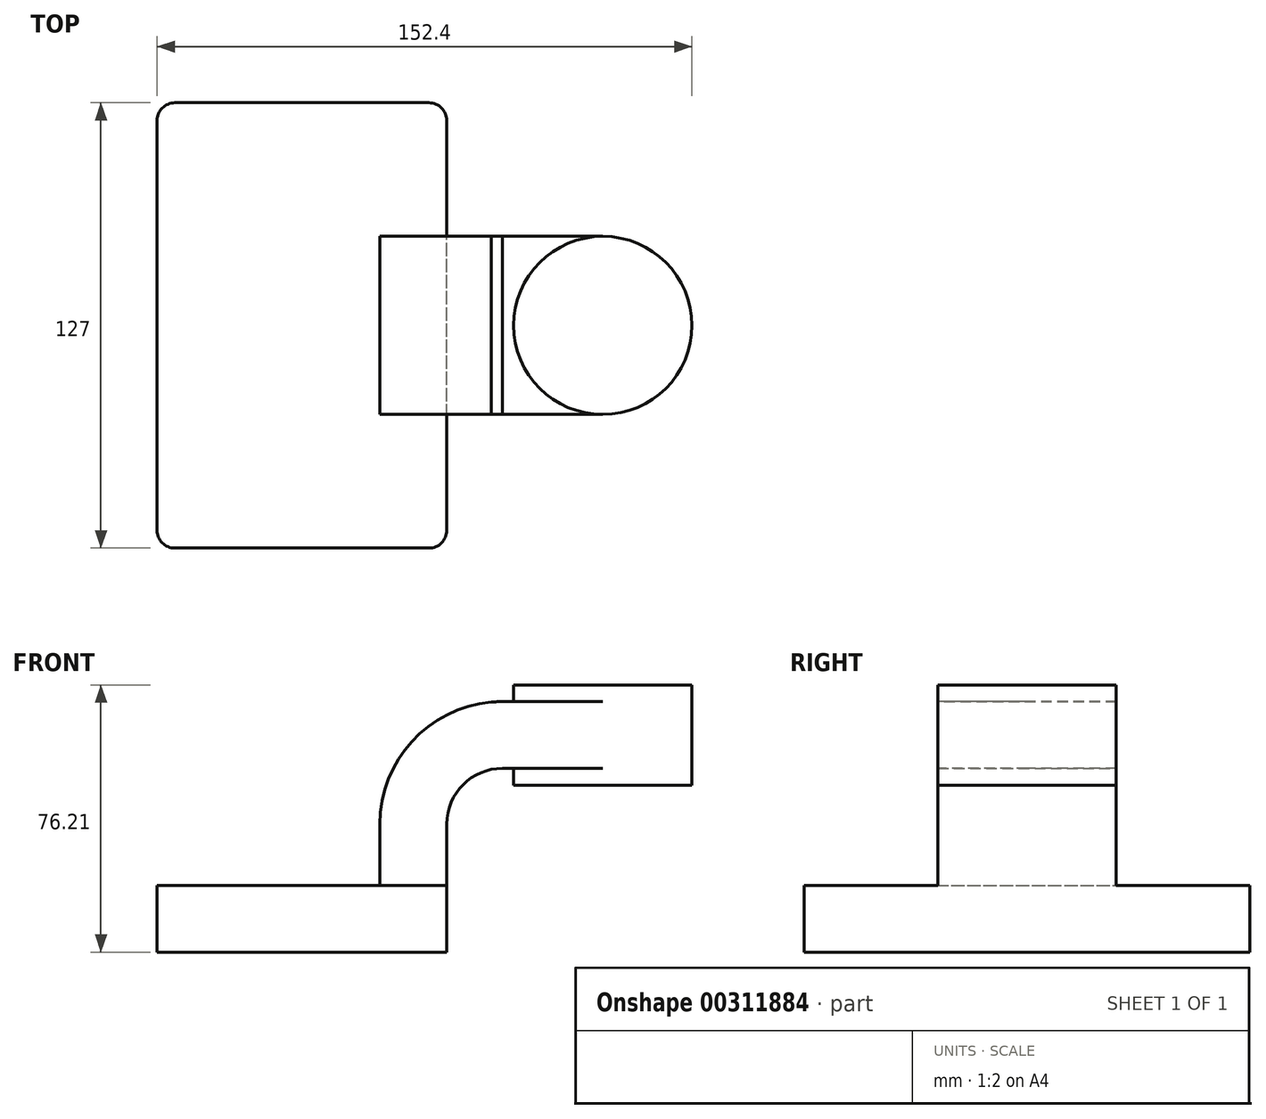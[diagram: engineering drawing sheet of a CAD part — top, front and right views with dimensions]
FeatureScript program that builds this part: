
annotation { "Feature Type Name" : "Feature", "Feature Type Description" : "" }
export const myFeature = defineFeature(function(context is Context, id is Id, definition is map)
    precondition{}
    {
        {
            var Q0;
            Q0=qCreatedBy(makeId("Front.planeOp"),FACE);
            var sketch = newSketch(context, id + "F0", { "sketchPlane" : qUnion([Q0])});
            skLineSegment(sketch, "E0.rect.bottom", {"start": v(-41.28, 9.52) * mm, "end": v(41.28, 9.52) * mm});
            skLineSegment(sketch, "E0.rect.top", {"start": v(-41.28, -9.52) * mm, "end": v(41.28, -9.52) * mm});
            skLineSegment(sketch, "E0.rect.left", {"start": v(-41.28, 9.52) * mm, "end": v(-41.28, -9.52) * mm});
            skLineSegment(sketch, "E0.rect.right", {"start": v(41.28, 9.52) * mm, "end": v(41.28, -9.52) * mm});
            skPoint(sketch, "E0.rect.middle", {"position": v(0, 0) * mm});
            skLineSegment(sketch, "E1", {"start": v(41.28, 9.52) * mm, "end": v(41.28, 27) * mm});
            skArc(sketch, "E2", {"start": v(41.28, 27) * mm, "mid": v(45.92, 38.23) * mm, "end": v(57.15, 42.88) * mm});
            skLineSegment(sketch, "E3", {"start": v(57.15, 42.88) * mm, "end": v(85.72, 42.88) * mm});
            skLineSegment(sketch, "E4.rect.bottom", {"start": v(60.32, 38.1) * mm, "end": v(111.12, 38.1) * mm});
            skLineSegment(sketch, "E4.rect.top", {"start": v(60.32, 66.68) * mm, "end": v(111.12, 66.68) * mm});
            skLineSegment(sketch, "E4.rect.left", {"start": v(60.32, 38.1) * mm, "end": v(60.32, 66.68) * mm});
            skLineSegment(sketch, "E4.rect.right", {"start": v(111.13, 38.1) * mm, "end": v(111.12, 66.68) * mm});
            skPoint(sketch, "E4.rect.middle", {"position": v(85.72, 52.39) * mm});
            skLineSegment(sketch, "E5.0", {"start": v(57.15, 61.93) * mm, "end": v(85.72, 61.93) * mm});
            skArc(sketch, "E5.1", {"start": v(22.23, 27) * mm, "mid": v(32.45, 51.7) * mm, "end": v(57.15, 61.93) * mm});
            skLineSegment(sketch, "E5.2", {"start": v(22.23, 9.52) * mm, "end": v(22.23, 27) * mm});
            skLineSegment(sketch, "E6", {"start": v(85.72, 38.1) * mm, "end": v(85.72, 66.68) * mm});
            skFitSpline(sketch, "E7", {"points": [v(-41.28, 9.53) * mm, v(57.15, 61.93) * mm], "startDerivative": vector(5.2, 92.34) * mm, "endDerivative": vector(120.92, 4.22) * mm});
            skSolve(sketch);
        }
        {
            var Q0;
            Q0=makeQuery(id+"F0.imprint","IMPRINT",FACE,{"disambiguationData":[TD([[makeQuery(id+"F0.imprint","IMPRINT",EDGE,{"derivedFrom":sQuery(id+"F0.wireOp",EDGE,"E0.rect.top")}),1.0]])]});
            extrude(context, id + "F1", {"entities" : qUnion([Q0]), "endBound" : BoundingType.SYMMETRIC, "depth" : 127 * mm});
        }
        {
            var Q0;
            {var subQ9=sQuery(id+"F0.wireOp",EDGE,"E1");Q0=makeQuery(id+"F0.imprint","IMPRINT",FACE,{"disambiguationData":[TD([[makeQuery(id+"F0.imprint","IMPRINT",EDGE,{"derivedFrom":subQ9}),1.0]])]});}
            var Q1;
            {var subQ0=sQuery(id+"F0.wireOp",EDGE,"E6");var subQ1=sQuery(id+"F0.wireOp",EDGE,"E3");var subQ2=makeQuery(id+"F0.imprint","INTERSECT",VERTEX,{"derivedFrom":[subQ1,subQ0]});Q1=makeQuery(id+"F0.imprint","IMPRINT",FACE,{"disambiguationData":[TD([[makeQuery(id+"F0.imprint","IMPRINT",EDGE,{"disambiguationData":[TD([[subQ2,1.0]])],"derivedFrom":subQ1}),1.0]])]});}
            extrude(context, id + "F2", {"entities" : qUnion([Q0, Q1]), "operationType" : NewBodyOperationType.ADD, "endBound" : BoundingType.SYMMETRIC, "depth" : 50.8 * mm});
        }
        {
            var Q0;
            {var subQ5=sQuery(id+"F0.wireOp",EDGE,"E4.rect.right");Q0=makeQuery(id+"F0.imprint","IMPRINT",FACE,{"disambiguationData":[TD([[makeQuery(id+"F0.imprint","IMPRINT",EDGE,{"derivedFrom":subQ5}),1.0]])]});}
            var Q1;
            Q1=sQuery(id+"F0.wireOp",EDGE,"E6");
            revolve(context, id + "F3", {"operationType" : NewBodyOperationType.ADD, "entities" : qUnion([Q0]), "axis" : qUnion([Q1]), "revolveType" : RevolveType.FULL});
        }
        {
            var Q0;
            Q0=makeQuery(id+"F1.opExtrude","CAP_EDGE",EDGE,{"disambiguationData":[OSD([sQuery(id+"F0.wireOp",EDGE,"E0.rect.right")])],"isStart":false});
            var Q1;
            Q1=makeQuery(id+"F1.opExtrude","CAP_EDGE",EDGE,{"disambiguationData":[OSD([sQuery(id+"F0.wireOp",EDGE,"E0.rect.left")])],"isStart":false});
            var Q2;
            Q2=makeQuery(id+"F1.opExtrude","CAP_EDGE",EDGE,{"disambiguationData":[OSD([sQuery(id+"F0.wireOp",EDGE,"E0.rect.right")])],"isStart":true});
            var Q3;
            Q3=makeQuery(id+"F1.opExtrude","CAP_EDGE",EDGE,{"disambiguationData":[OSD([sQuery(id+"F0.wireOp",EDGE,"E0.rect.left")])],"isStart":true});
            fillet(context, id + "F4", {"entities" : qUnion([Q0, Q1, Q2, Q3]), "radius" : 5.08 * mm, "tangentPropagation" : true, "allowEdgeOverflow" : false});
        }
    });
